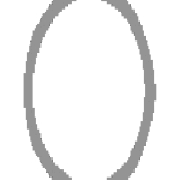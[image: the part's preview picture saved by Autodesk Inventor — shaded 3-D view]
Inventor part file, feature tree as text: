
AUTODESK INVENTOR PART (.ipt)
format: ipt  version: 2021 (Build 250183000, 183)  size: 115,712 bytes
history: native  units: in
note: dims shown in document units (in); Inventor stores cm internally (conversion verified against a paired STEP export)
features: other x4, sketch x3, plane x1
ambient origin geometry x8: Origin, YZ Plane, XZ Plane, XY Plane, X Axis, Y Axis, Z Axis, Center Point
bodies: Solid1 (feature_tree), Body (feature_tree)
feature tree (8):
  other  "Driven Length"
  other  "Frame Generator"
  other  "Start Plane"
  other  "End Plane"
  sketch  "Sketch"  dims[d2=0.5in d4=-0.0in d5=0.5in d6=0.12in d7=0.0in d8=90.0deg d9=0.5in]
  sketch  "Sketch2"  dims[d0=1.0in]
  plane  "Work Plane3"
  sketch  "Sketch3"  dims[d1=0.065in]
